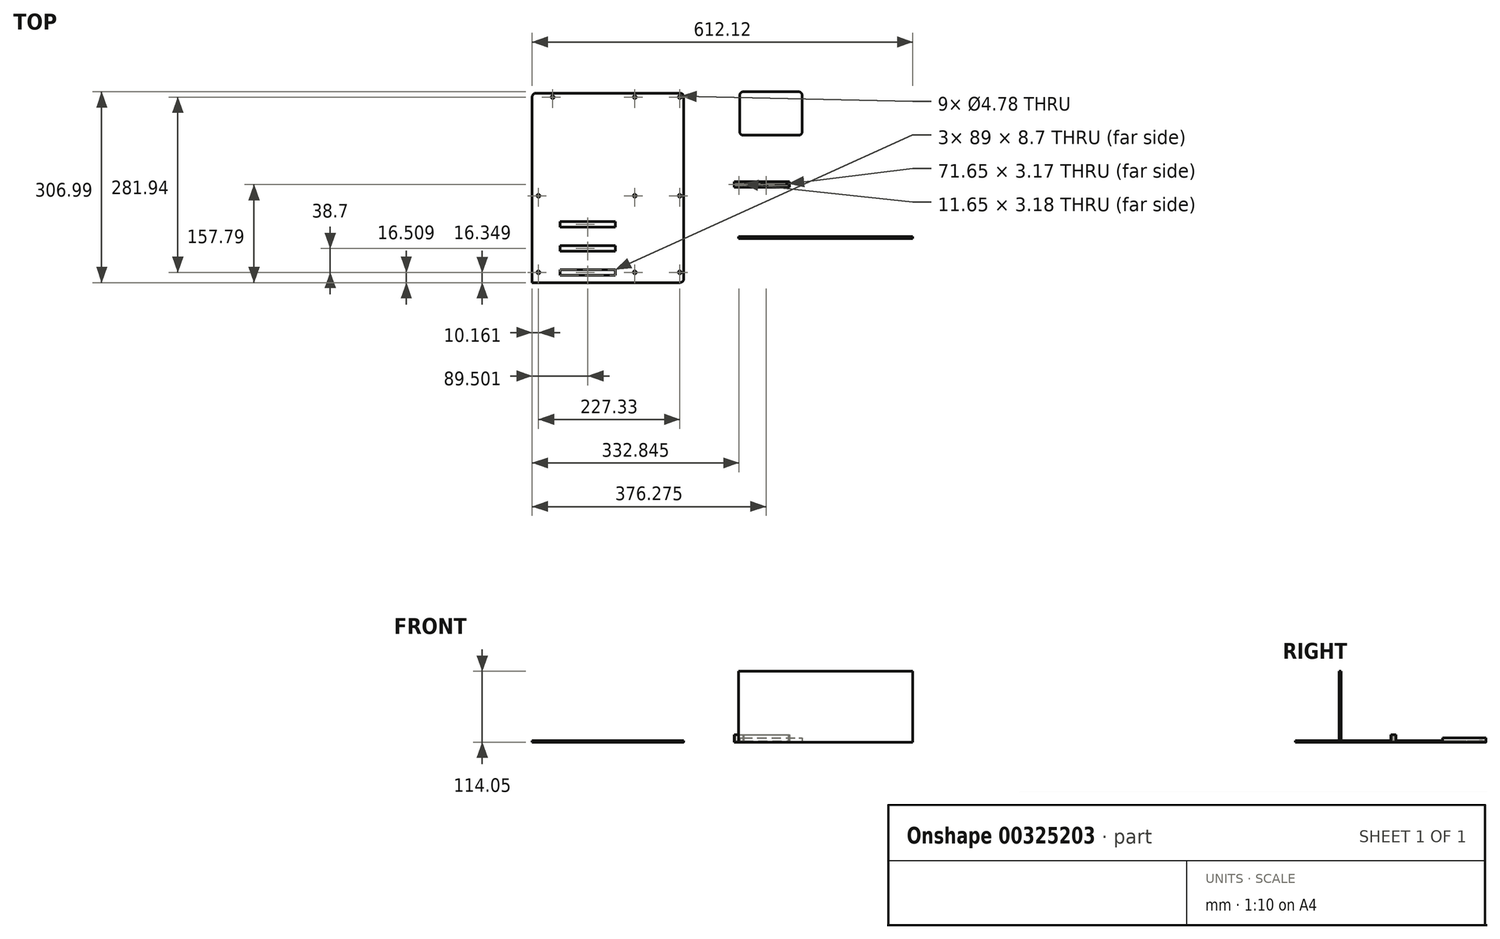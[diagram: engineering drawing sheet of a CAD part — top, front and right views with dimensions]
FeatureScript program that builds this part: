
annotation { "Feature Type Name" : "Feature", "Feature Type Description" : "" }
export const myFeature = defineFeature(function(context is Context, id is Id, definition is map)
    precondition{}
    {
        {
            var Q0;
            Q0=qCreatedBy(makeId("Top.planeOp"),FACE);
            var sketch = newSketch(context, id + "F0", { "sketchPlane" : qUnion([Q0])});
            skLineSegment(sketch, "E0.bottom", {"start": v(109.15, -162.14) * mm, "end": v(-128.34, -162.14) * mm});
            skLineSegment(sketch, "E0.top", {"start": v(109.15, 142.66) * mm, "end": v(-128.34, 142.66) * mm});
            skLineSegment(sketch, "E0.left", {"start": v(115.5, -155.8) * mm, "end": v(115.5, 136.3) * mm});
            skLineSegment(sketch, "E0.right", {"start": v(-128.34, -162.14) * mm, "end": v(-128.34, 136.3) * mm});
            skCircle(sketch, "E1", {"center": v(-118.18, -145.63) * mm, "radius": 2.39 * mm});
            skCircle(sketch, "E2", {"center": v(109.15, -145.63) * mm, "radius": 2.39 * mm});
            skCircle(sketch, "E3", {"center": v(36.76, -145.63) * mm, "radius": 2.39 * mm});
            skLineSegment(sketch, "E4", {"start": v(-128.34, -162.14) * mm, "end": v(-118.18, -162.14) * mm});
            skCircle(sketch, "E5", {"center": v(109.15, -22.44) * mm, "radius": 2.39 * mm});
            skCircle(sketch, "E6", {"center": v(109.15, 136.3) * mm, "radius": 2.39 * mm});
            skCircle(sketch, "E7", {"center": v(-118.18, -22.44) * mm, "radius": 2.39 * mm});
            skCircle(sketch, "E8", {"center": v(36.76, -22.44) * mm, "radius": 2.39 * mm});
            skCircle(sketch, "E9", {"center": v(36.76, 136.3) * mm, "radius": 2.39 * mm});
            skLineSegment(sketch, "E10", {"start": v(-121.99, 142.66) * mm, "end": v(-95.32, 142.66) * mm});
            skCircle(sketch, "E11", {"center": v(-95.32, 136.3) * mm, "radius": 2.39 * mm});
            skPoint(sketch, "E12.visualSharp", {"position": v(115.5, 142.66) * mm});
            skArc(sketch, "E12.filletArc", {"start": v(115.5, 136.3) * mm, "mid": v(113.64, 140.8) * mm, "end": v(109.15, 142.66) * mm});
            skPoint(sketch, "E13.visualSharp", {"position": v(115.5, -162.14) * mm});
            skArc(sketch, "E13.filletArc", {"start": v(109.15, -162.14) * mm, "mid": v(113.64, -160.28) * mm, "end": v(115.5, -155.8) * mm});
            skPoint(sketch, "E14.visualSharp", {"position": v(-128.34, 142.66) * mm});
            skArc(sketch, "E14.filletArc", {"start": v(-121.99, 142.66) * mm, "mid": v(-126.48, 140.8) * mm, "end": v(-128.34, 136.3) * mm});
            skLineSegment(sketch, "E15.bottom", {"start": v(-83.34, -141.44) * mm, "end": v(5.66, -141.44) * mm});
            skLineSegment(sketch, "E15.top", {"start": v(-83.34, -150.14) * mm, "end": v(5.66, -150.14) * mm});
            skLineSegment(sketch, "E15.left", {"start": v(-83.34, -141.44) * mm, "end": v(-83.34, -150.14) * mm});
            skLineSegment(sketch, "E15.right", {"start": v(5.66, -141.44) * mm, "end": v(5.66, -150.14) * mm});
            skLineSegment(sketch, "E16.bottom", {"start": v(-83.34, -102.74) * mm, "end": v(5.66, -102.74) * mm});
            skLineSegment(sketch, "E16.top", {"start": v(-83.34, -111.44) * mm, "end": v(5.66, -111.44) * mm});
            skLineSegment(sketch, "E16.left", {"start": v(-83.34, -102.74) * mm, "end": v(-83.34, -111.44) * mm});
            skLineSegment(sketch, "E16.right", {"start": v(5.66, -102.74) * mm, "end": v(5.66, -111.44) * mm});
            skLineSegment(sketch, "E17.bottom", {"start": v(-83.34, -64.04) * mm, "end": v(5.66, -64.04) * mm});
            skLineSegment(sketch, "E17.top", {"start": v(-83.34, -72.74) * mm, "end": v(5.66, -72.74) * mm});
            skLineSegment(sketch, "E17.left", {"start": v(-83.34, -64.04) * mm, "end": v(-83.34, -72.74) * mm});
            skLineSegment(sketch, "E17.right", {"start": v(5.66, -64.04) * mm, "end": v(5.66, -72.74) * mm});
            skSolve(sketch);
        }
        {
            var Q0;
            Q0 = qSketchRegion(id + "F0", true);
            extrude(context, id + "F1", {"entities" : qUnion([Q0]), "depth" : 2.54 * mm});
        }
        {
            var Q0;
            Q0=qCreatedBy(makeId("Top.planeOp"),FACE);
            var sketch = newSketch(context, id + "F2", { "sketchPlane" : qUnion([Q0])});
            skLineSegment(sketch, "E18.bottom", {"start": v(196.72, 0) * mm, "end": v(285.72, 0) * mm});
            skLineSegment(sketch, "E18.top", {"start": v(196.72, -8.7) * mm, "end": v(285.72, -8.7) * mm});
            skLineSegment(sketch, "E18.left", {"start": v(196.72, 0) * mm, "end": v(196.72, -8.7) * mm});
            skLineSegment(sketch, "E18.right", {"start": v(285.72, 0) * mm, "end": v(285.72, -8.7) * mm});
            skLineSegment(sketch, "E19.bottom", {"start": v(198.68, -2.76) * mm, "end": v(210.33, -2.76) * mm});
            skLineSegment(sketch, "E19.top", {"start": v(198.68, -5.94) * mm, "end": v(210.33, -5.94) * mm});
            skLineSegment(sketch, "E19.left", {"start": v(198.68, -2.76) * mm, "end": v(198.68, -5.94) * mm});
            skLineSegment(sketch, "E19.right", {"start": v(210.33, -2.76) * mm, "end": v(210.33, -5.94) * mm});
            skLineSegment(sketch, "E20.bottom", {"start": v(212.1, -2.76) * mm, "end": v(283.76, -2.76) * mm});
            skLineSegment(sketch, "E20.top", {"start": v(212.1, -5.94) * mm, "end": v(283.76, -5.94) * mm});
            skLineSegment(sketch, "E20.left", {"start": v(212.1, -2.76) * mm, "end": v(212.1, -5.94) * mm});
            skLineSegment(sketch, "E20.right", {"start": v(283.76, -2.76) * mm, "end": v(283.76, -5.94) * mm});
            skLineSegment(sketch, "E21.bottom", {"start": v(210.66, 75) * mm, "end": v(300.66, 75) * mm});
            skLineSegment(sketch, "E21.top", {"start": v(210.66, 144.85) * mm, "end": v(300.66, 144.85) * mm});
            skLineSegment(sketch, "E21.left", {"start": v(205.66, 80) * mm, "end": v(205.66, 139.85) * mm});
            skLineSegment(sketch, "E21.right", {"start": v(305.66, 80) * mm, "end": v(305.66, 139.85) * mm});
            skPoint(sketch, "E22.visualSharp", {"position": v(205.66, 144.85) * mm});
            skArc(sketch, "E22.filletArc", {"start": v(210.66, 144.85) * mm, "mid": v(207.13, 143.38) * mm, "end": v(205.66, 139.85) * mm});
            skPoint(sketch, "E23.visualSharp", {"position": v(205.66, 75) * mm});
            skArc(sketch, "E23.filletArc", {"start": v(205.66, 80) * mm, "mid": v(207.13, 76.46) * mm, "end": v(210.66, 75) * mm});
            skPoint(sketch, "E24.visualSharp", {"position": v(305.66, 75) * mm});
            skArc(sketch, "E24.filletArc", {"start": v(300.66, 75) * mm, "mid": v(304.2, 76.46) * mm, "end": v(305.66, 80) * mm});
            skPoint(sketch, "E25.visualSharp", {"position": v(305.66, 144.85) * mm});
            skArc(sketch, "E25.filletArc", {"start": v(305.66, 139.85) * mm, "mid": v(304.2, 143.38) * mm, "end": v(300.66, 144.85) * mm});
            skLineSegment(sketch, "E26.bottom", {"start": v(203.87, -88.33) * mm, "end": v(483.78, -88.33) * mm});
            skLineSegment(sketch, "E26.top", {"start": v(203.87, -91.5) * mm, "end": v(483.78, -91.5) * mm});
            skLineSegment(sketch, "E26.left", {"start": v(203.87, -88.33) * mm, "end": v(203.87, -91.5) * mm});
            skLineSegment(sketch, "E26.right", {"start": v(483.78, -88.33) * mm, "end": v(483.78, -91.5) * mm});
            skSolve(sketch);
        }
        {
            var Q0;
            Q0=makeQuery(id+"F2.imprint","IMPRINT",FACE,{"disambiguationData":[TD([[makeQuery(id+"F2.imprint","IMPRINT",EDGE,{"derivedFrom":sQuery(id+"F2.wireOp",EDGE,"E19.bottom")}),-1.0]])]});
            var Q1;
            Q1=makeQuery(id+"F2.imprint","IMPRINT",FACE,{"disambiguationData":[TD([[makeQuery(id+"F2.imprint","IMPRINT",EDGE,{"derivedFrom":sQuery(id+"F2.wireOp",EDGE,"E20.bottom")}),-1.0]])]});
            extrude(context, id + "F3", {"entities" : qUnion([Q0, Q1]), "depth" : 1.5 * mm});
        }
        {
            var Q0;
            Q0=makeQuery(id+"F2.imprint","IMPRINT",FACE,{"disambiguationData":[TD([[makeQuery(id+"F2.imprint","IMPRINT",EDGE,{"derivedFrom":sQuery(id+"F2.wireOp",EDGE,"E18.bottom")}),-1.0]])]});
            extrude(context, id + "F4", {"entities" : qUnion([Q0]), "depth" : 12 * mm});
        }
        {
            var Q0;
            Q0=makeQuery(id+"F2.imprint","IMPRINT",FACE,{"disambiguationData":[TD([[makeQuery(id+"F2.imprint","IMPRINT",EDGE,{"derivedFrom":sQuery(id+"F2.wireOp",EDGE,"E21.bottom")}),1.0]])]});
            extrude(context, id + "F5", {"entities" : qUnion([Q0]), "depth" : 7 * mm});
        }
        {
            var Q0;
            Q0=makeQuery(id+"F2.imprint","IMPRINT",FACE,{"disambiguationData":[TD([[makeQuery(id+"F2.imprint","IMPRINT",EDGE,{"derivedFrom":sQuery(id+"F2.wireOp",EDGE,"E26.bottom")}),-1.0]])]});
            extrude(context, id + "F6", {"entities" : qUnion([Q0]), "depth" : 114.05 * mm});
        }
    });
